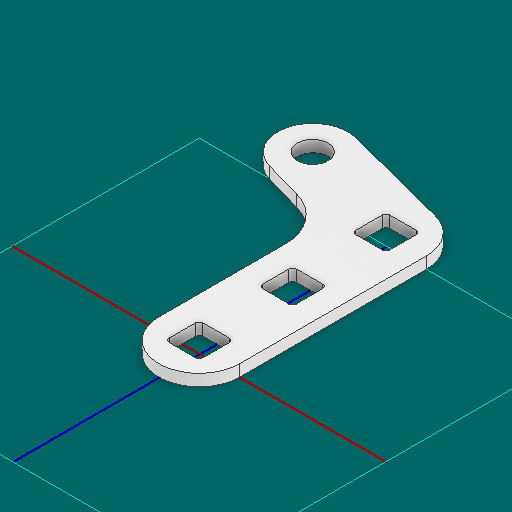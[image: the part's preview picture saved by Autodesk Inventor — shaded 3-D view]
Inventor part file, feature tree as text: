
AUTODESK INVENTOR PART (.ipt)
format: ipt  version: 2025 (Build 290162000, 162)  size: 162,304 bytes
history: native  units: in
note: dims shown in document units (in); Inventor stores cm internally (conversion verified against a paired STEP export)
features: other x5, hole x4, sketch x1
ambient origin geometry x8: Origin, YZ Plane, XZ Plane, XY Plane, X Axis, Y Axis, Z Axis, Center Point
bodies: Solid1 (feature_tree)
feature tree (10):
  other  "bent_gusset_improved.ipt"
  other  "Blocks"
  hole  "hole"  [1 undecoded]
  other  "main"
  other  "Solid1::bent_gusset_improved.ipt"
  other  "TaggingFeature1"
  sketch  "Sketch1"  dims[d0=0.3937in d6=0.182in d7=0.182in d8=0.02in d9=0.5in d10=0.5in d12=0.675in]
  hole  "hole:1"  [1 undecoded]
  hole  "hole:2"  [1 undecoded]
  hole  "hole:3"  [1 undecoded]
note: 4 required parameter values undecoded (feature->parameter linkage not recoverable at this tier; creation-order binding heuristic only, values carry confidence <= 0.55)
